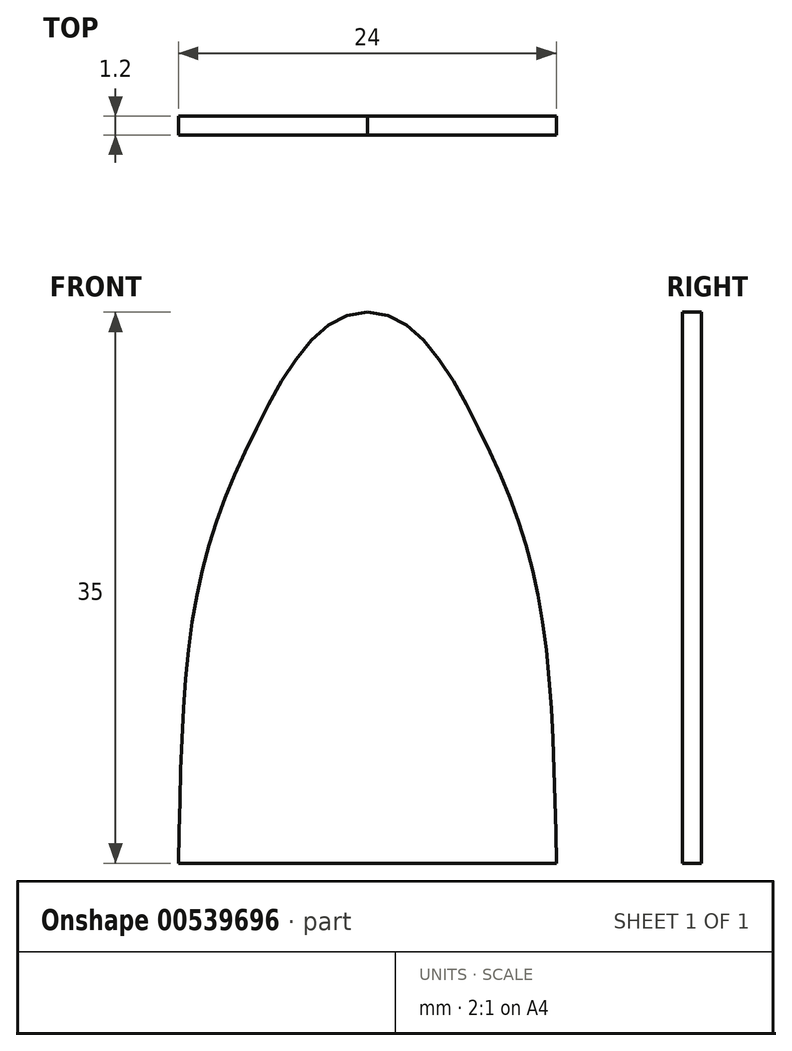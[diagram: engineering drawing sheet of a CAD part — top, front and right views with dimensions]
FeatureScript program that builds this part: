
annotation { "Feature Type Name" : "Feature", "Feature Type Description" : "" }
export const myFeature = defineFeature(function(context is Context, id is Id, definition is map)
    precondition{}
    {
        {
            var Q0;
            Q0=qCreatedBy(makeId("Front.planeOp"),FACE);
            var sketch = newSketch(context, id + "F0", { "sketchPlane" : qUnion([Q0])});
            skFitSpline(sketch, "E0", {"points": [v(12, 0) * mm, v(10.9, 16.72) * mm, v(6.86, 28.01) * mm, v(0, 35) * mm], "startDerivative": vector(-0.96, 45.35) * mm, "endDerivative": vector(-31.02, -0.74) * mm});
            skFitSpline(sketch, "E1.MirrorCS", {"points": [v(-12, 0) * mm, v(-10.9, 16.72) * mm, v(-6.86, 28.01) * mm, v(0, 35) * mm], "startDerivative": vector(0.96, 45.35) * mm, "endDerivative": vector(31.02, -0.74) * mm});
            skLineSegment(sketch, "E2", {"start": v(12, 0) * mm, "end": v(-12, 0) * mm});
            skSolve(sketch);
        }
        {
            var Q0;
            Q0=makeQuery(id+"F0.imprint","IMPRINT",FACE,{"disambiguationData":[TD([[makeQuery(id+"F0.imprint","IMPRINT",EDGE,{"derivedFrom":sQuery(id+"F0.wireOp",EDGE,"E0")}),1.0]])]});
            extrude(context, id + "F1", {"entities" : qUnion([Q0]), "depth" : 1.2 * mm, "offsetDistance" : 25 * mm});
        }
    });
